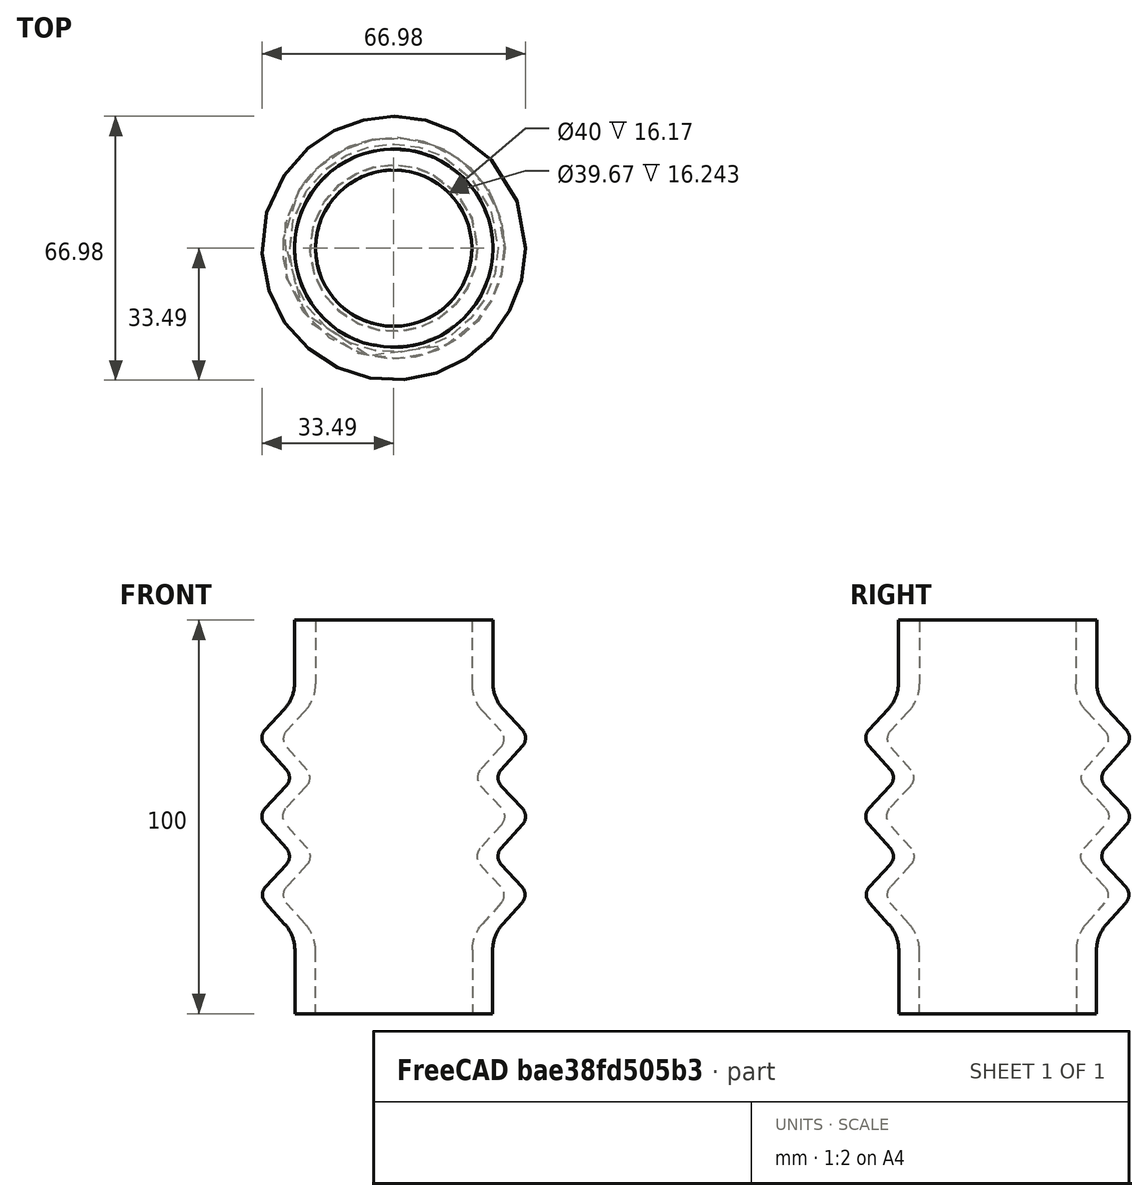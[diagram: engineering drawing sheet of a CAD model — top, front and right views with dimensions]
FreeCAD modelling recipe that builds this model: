
FCSTD DOCUMENT  (FreeCAD 0.14R2756 (Git))
Label: Bellows_coupling
License: CC-BY 3.0
LicenseURL: http://creativecommons.org/licenses/by/3.0/
objects: PartDesign::Fillet×2, Sketcher::SketchObject×1, PartDesign::Revolution×1
note: 5 computed .brp shape members not serialized (recipe doc carries the construction recipe); baked Part::Feature solids carry a one-line shape summary decoded from their .brp

FEATURE [Sketcher::SketchObject] Sketch
  Placement = pos=(0,0,0) rot=(-1,0,0;4.71239rad)
  sketch-geometry (21):
    g0: LineSegment StartX=25.1196 StartY=0 StartZ=0 EndX=25.1196 EndY=19.8892 EndZ=0
    g1: LineSegment StartX=25.1196 StartY=19.8892 StartZ=0 EndX=34.4114 EndY=30.2397 EndZ=0
    g2: LineSegment StartX=34.4114 StartY=30.2397 StartZ=0 EndX=25.4228 EndY=39.9287 EndZ=0
    g3: LineSegment StartX=25.4228 StartY=39.9287 StartZ=0 EndX=34.5487 EndY=50.0945 EndZ=0
    g4: LineSegment StartX=34.5487 StartY=50.0945 StartZ=0 EndX=25.4326 EndY=59.921 EndZ=0
    g5: LineSegment StartX=25.4326 StartY=59.921 StartZ=0 EndX=34.5518 EndY=70.0793 EndZ=0
    g6: LineSegment StartX=34.5518 StartY=70.0793 StartZ=0 EndX=25.1836 EndY=80.1774 EndZ=0
    g7: LineSegment StartX=25.1836 StartY=80.1774 StartZ=0 EndX=25.1836 EndY=100 EndZ=0
    g8: LineSegment StartX=25.1836 StartY=100 StartZ=0 EndX=19.8354 EndY=100 EndZ=0
    g9: LineSegment StartX=19.8354 StartY=100 StartZ=0 EndX=19.8354 EndY=79.8324 EndZ=0
    g10: LineSegment StartX=19.8354 StartY=79.8324 StartZ=0 EndX=27.2547 EndY=71.8351 EndZ=0
    g11: LineSegment StartX=27.2878 StartY=67.7907 StartZ=0 EndX=20.2175 EndY=59.9148 EndZ=0
    g12: LineSegment StartX=20.2175 StartY=59.9148 StartZ=0 EndX=27.4326 EndY=52.1376 EndZ=0
    g13: LineSegment StartX=27.4657 StartY=48.0932 StartZ=0 EndX=20.1092 EndY=39.8985 EndZ=0
    g14: LineSegment StartX=20.1092 StartY=39.8985 StartZ=0 EndX=27.27 EndY=32.1797 EndZ=0
    g15: LineSegment StartX=27.3031 StartY=28.1353 StartZ=0 EndX=20 EndY=20 EndZ=0
    g16: LineSegment StartX=20 StartY=20 StartZ=0 EndX=20 EndY=0 EndZ=0
    g17: LineSegment StartX=20 StartY=0 StartZ=0 EndX=25.1196 EndY=0 EndZ=0
    g18: ArcOfCircle CenterX=25.0553 CenterY=69.7947 CenterZ=0 NormalX=0 NormalY=0 NormalZ=1 Radius=3 StartAngle=5.55164 EndAngle=7.0311
    g19: ArcOfCircle CenterX=25.2332 CenterY=50.0973 CenterZ=0 NormalX=0 NormalY=0 NormalZ=1 Radius=3 StartAngle=5.55164 EndAngle=7.0311
    g20: ArcOfCircle CenterX=25.0707 CenterY=30.1394 CenterZ=0 NormalX=0 NormalY=0 NormalZ=1 Radius=3 StartAngle=5.55164 EndAngle=7.0311
  constraints (42):
    c: PointOnObject(g0,g-1)
    c: Vertical(g0)
    c: Coincident(g0,g1)
    c: Coincident(g1,g2)
    c: Coincident(g2,g3)
    c: Coincident(g3,g4)
    c: Coincident(g4,g5)
    c: Coincident(g5,g6)
    c: Coincident(g6,g7)
    c: Vertical(g7)
    c: Coincident(g7,g8)
    c: Horizontal(g8)
    c: Coincident(g8,g9)
    c: Vertical(g9)
    c: Coincident(g9,g10)
    c: Coincident(g11,g12)
    c: Coincident(g13,g14)
    c: Coincident(g15,g16)
    c: PointOnObject(g16,g-1)
    c: Vertical(g16)
    c: Coincident(g16,g17)
    c: Coincident(g17,g0)
    c: DistanceY(g8,g16) = -100
    c: Tangent(g10,g18)
    c: Tangent(g11,g18)
    c: Tangent(g12,g19)
    c: Tangent(g13,g19)
    c: Tangent(g14,g20)
    c: Tangent(g15,g20)
    c: Equal(g20,g19)
    c: Equal(g19,g18)
    c: Radius(g18) = 3
    c: Parallel(g15,g13)
    c: Parallel(g13,g11)
    c: Parallel(g11,g5)
    c: Parallel(g5,g3)
    c: Parallel(g3,g1)
    c: Parallel(g10,g6)
    c: Parallel(g6,g12)
    c: Parallel(g12,g4)
    c: Parallel(g4,g14)
    c: Parallel(g14,g2)
FEATURE [PartDesign::Revolution] Revolution
  Angle = 360
  Axis = (0,0,1)
  Base = (0,0,0)
  Placement = pos=(0,0,0) rot=(-1,0,0;4.71239rad)
  ReferenceAxis = -> Sketch [V_Axis]
  Reversed = true
  Sketch = -> Sketch
FEATURE [PartDesign::Fillet] Fillet
  Base = -> Revolution [Edge17,Edge15,Edge13,Edge11,Edge9,Edge30,Edge36]
  Placement = pos=(0,0,0) rot=(-1,0,0;4.71239rad)
  Radius = 3
FEATURE [PartDesign::Fillet] Fillet001
  Base = -> Fillet [Edge3,Edge40,Edge50,Edge13]
  Placement = pos=(0,0,0) rot=(-1,0,0;4.71239rad)
  Radius = 10
